# Revit family: PRD_FrankeWS_WstBns_RODANWasteDisposalFlap_RODX605TT
name_source: partatom
category: Specialty Equipment
revit_build: Autodesk Revit 2018 (Build: 20190510_1515(x64)
units: mm (PartAtom-declared; Revit-internal decimal feet)

## family parameters
Cut with Voids When Loaded = Yes
Host = Face
OmniClass Number = 23.40.20.31.11
OmniClass Title = Bins
Part Type = Normal
Room Calculation Point = No
Round Connector Dimension = Use Diameter
Shared = No

## types (1)
- RODX605TT
    AssetType = Fixed
    BIMObjectName = PRD_AR_WasteBins_RODANWasteDisposalFlap_RODX605TT
    Category = Pr_40_50_07_96, Waste bins
    Default Elevation = 1000 mm  [stored 3.28084 ft]
    Description = Waste disposal flap for table top installation, stainless steel, visible surfaces satin finished, material thickness 0.8 mm, self-closing disposal flap, without waste container.
    DispenserMaterial = PRD_AR_StainlessSteel_SatinFinished
    DurationUnit = year
    Features = stainless steel, surface satin finished
    Finish = satin finished
    GrossWeight = 1.20 kg
    IfcExportAs = IfcFurnitureType
    IfcExportType = USERDEFINED
    IsBuiltIn = TRUE
    MainColor = stainless steel
    Manufacturer = KWC Group AG
    ManufacturerName = KWC Group AG
    ManufacturerURL = www.kwc.com
    Material = stainless steel
    MaterialCode = 1.4301
    MaterialThickness = 0.80 mm
    Model = RODX605TT
    ModelNumber = 2000101211
    ModelReference = RODX605TT
    NBSDescription = Waste bins
    NBSReference = 45-35-72/380
    Name = Waste Disposal Flap RODX605TT
    NetWeight = 1.00 kg
    NominalDepth = 195 mm  [stored 0.639764 ft]
    NominalHeight = 53 mm  [stored 0.173885 ft]
    NominalWidth = 330 mm  [stored 1.08268 ft]
    ProductInformation = https://pim.kwc.com
    Size = 330 x 53 x 195 mm
    TypeOfFixing = Screw-glue
    TypeOfMounting = Counter top mounting
    URL = www.kwc.com
    Uniclass2015Code = Pr_40_50_07_96
    Uniclass2015Title = Waste bins
    Uniclass2015Version = Products v1.10
    Version = 1
    WarrantyDurationUnit = year

note: [stored X ft] marks values corroborated as IEEE doubles in the binary element streams (Revit-internal decimal feet)

## geometry (parser evidence)
native form markers: Sweep x3
no freeform markers — native parametric forms only
